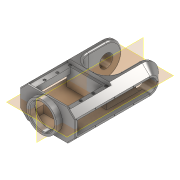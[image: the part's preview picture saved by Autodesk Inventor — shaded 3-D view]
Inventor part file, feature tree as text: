
AUTODESK INVENTOR PART (.ipt)
format: ipt  version: 2020.3 (Build 243373010, 373A)  size: 544,768 bytes
history: native  units: mm
features: sketch x10, extrude x10, fillet x5, chamfer x5, projected_geometry x5, mirror x2, hole x2
ambient origin geometry x8: Origin, YZ Plane, XZ Plane, XY Plane, X Axis, Y Axis, Z Axis, Center Point
bodies: Solid1 (feature_tree)
feature tree (39):
  sketch  "Sketch1"  dims[d0=80.0mm d1=65.0mm]
  extrude  "Extrusion1"  Depth=80.0mm
  extrude  "Extrusion2"  Depth=15.0mm TaperAngle=0.0deg
  extrude  "Extrusion3"  Depth=30.0mm
  fillet  "Fillet1"  Radius=145.0mm
  chamfer  "Chamfer1"  Distance=85.0mm
  fillet  "Fillet4"  Radius=42.5mm
  fillet  "Fillet5"  Radius=35.0mm
  chamfer  "Chamfer2"  Distance=2.0mm Angle=45.0deg
  chamfer  "Chamfer3"  Distance=2.0mm Angle=45.0deg
  extrude  "Extrusion4"  Depth=7.0mm
  sketch  "Sketch4"  dims[d9=30.0mm]
  extrude  "Extrusion5"  Depth=85.0mm TaperAngle=0.0deg
  extrude  "Extrusion6"  TaperAngle=0.0deg  [1 undecoded]
  mirror  "Mirror1"
  extrude  "Extrusion8"  Depth=20.0mm TaperAngle=0.0deg
  sketch  "Sketch5"  dims[d10=240.0mm d11=85.0mm d12=0.0mm d13=42.5mm]
  hole  "Hole1"  [1 undecoded]
  hole  "Hole2"  [1 undecoded]
  mirror  "Mirror3"
  extrude  "Extrusion9"  Depth=5.0mm
  chamfer  "Chamfer4"  Distance=5.0mm
  chamfer  "Chamfer5"  Distance=5.0mm
  fillet  "Fillet6"  Radius=33.5mm
  fillet  "Fillet7"  Radius=109.132594mm
  extrude  "Extrusion10"  Depth=10.0mm
  extrude  "Extrusion11"  Depth=10.0mm
  sketch  "Sketch2"  dims[d2=15.0mm d3=0.0mm d4=65.0mm d5=0.0mm]
  sketch  "Sketch3"  dims[d6=175.0mm d7=30.0mm d8=145.0mm]
  projected_geometry  "Projected Loop1"
  projected_geometry  "Projected Loop2"
  sketch  "Sketch6"  dims[d14=20.0mm d15=2.0mm d16=45.0deg d19=35.0mm]
  sketch  "Sketch7"  dims[d20=5.0mm d21=2.0mm d22=2.0mm d23=45.0deg d24=2.0mm d25=2.0mm d26=45.0deg]
  sketch  "Sketch8"  dims[d27=95.0mm d28=7.0mm]
  projected_geometry  "Projected Loop3"
  sketch  "Sketch11"  dims[d31=85.0mm d32=85.0mm d33=0.0mm]
  projected_geometry  "Projected Loop7"
  sketch  "Sketch13"  dims[d34=5.0mm d35=0.0mm d36=0.0mm d37=20.0mm d38=0.0mm d41=0.0mm d42=0.0mm d43=10.0mm d44=5.0mm d45=5.0mm d46=5.0mm d47=33.5mm d48=109.132594mm d49=33.5mm d50=33.5mm d51=7.132594mm d52=6.917mm d53=12.5mm d54=4.0mm d55=2.0mm d56=90.0deg d57=15.0mm d58=20.594885mm d59=5.0mm d61=5.0mm d62=2.5mm d63=2.5mm d64=2.5mm d65=50.0mm d66=50.0mm d67=50.0mm d68=43.0mm d69=20.0mm d70=2.459mm d71=6.0mm d72=4.0mm d73=2.0mm d74=90.0deg d75=8.8mm d76=20.594885mm d77=10.0mm d78=0.0mm d79=5.0mm d80=2.0mm d81=45.0deg d82=5.0mm d83=2.0mm d84=45.0deg d85=4.74mm d86=5.0mm d88=10.0mm d89=0.0mm d92=5.0mm d93=70.65mm d94=10.0mm d95=0.0mm]
  projected_geometry  "Projected Loop9"
note: 3 required parameter values undecoded (feature->parameter linkage not recoverable at this tier; creation-order binding heuristic only, values carry confidence <= 0.55)
